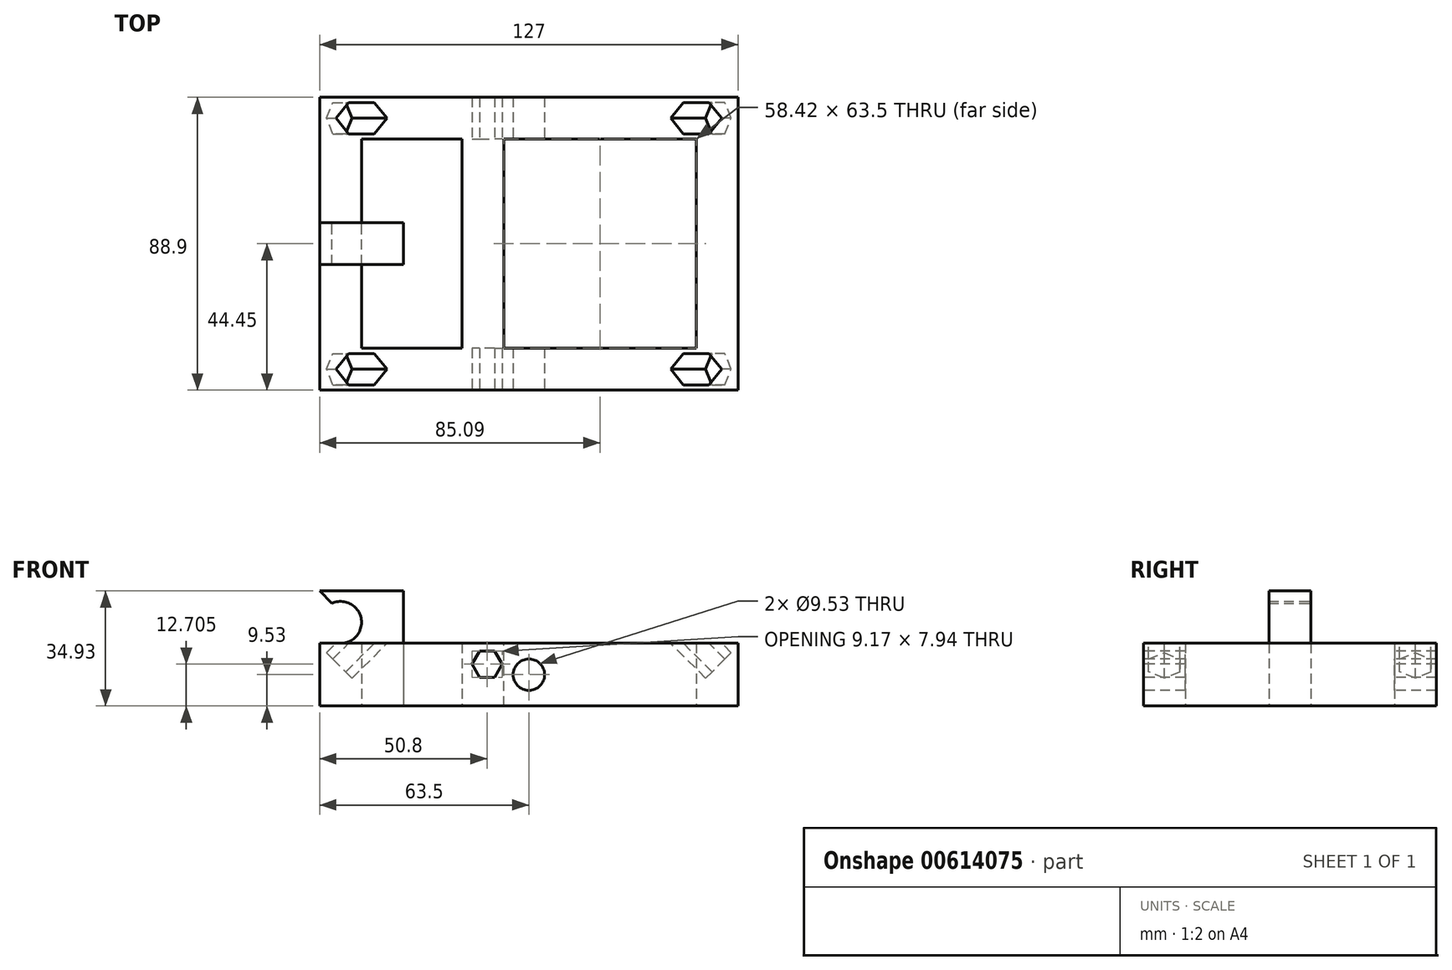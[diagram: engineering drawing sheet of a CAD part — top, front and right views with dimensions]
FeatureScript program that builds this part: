
annotation { "Feature Type Name" : "Feature", "Feature Type Description" : "" }
export const myFeature = defineFeature(function(context is Context, id is Id, definition is map)
    precondition{}
    {
        {
            var Q0;
            Q0=qCreatedBy(makeId("Top.planeOp"),FACE);
            var sketch = newSketch(context, id + "F0", { "sketchPlane" : qUnion([Q0])});
            skLineSegment(sketch, "E0.bottom", {"start": v(63.5, -44.45) * mm, "end": v(-63.5, -44.45) * mm});
            skLineSegment(sketch, "E0.top", {"start": v(63.5, 44.45) * mm, "end": v(-63.5, 44.45) * mm});
            skLineSegment(sketch, "E0.left", {"start": v(63.5, -44.45) * mm, "end": v(63.5, 44.45) * mm});
            skLineSegment(sketch, "E0.right", {"start": v(-63.5, -44.45) * mm, "end": v(-63.5, 44.45) * mm});
            skPoint(sketch, "E0.middle", {"position": v(0, 0) * mm});
            skLineSegment(sketch, "E1.bottom", {"start": v(50.8, -31.75) * mm, "end": v(-50.8, -31.75) * mm});
            skLineSegment(sketch, "E1.top", {"start": v(50.8, 31.75) * mm, "end": v(-50.8, 31.75) * mm});
            skLineSegment(sketch, "E1.left", {"start": v(50.8, -31.75) * mm, "end": v(50.8, 31.75) * mm});
            skLineSegment(sketch, "E1.right", {"start": v(-50.8, -31.75) * mm, "end": v(-50.8, 31.75) * mm});
            skLineSegment(sketch, "E2", {"start": v(0, -62.32) * mm, "end": v(0, 53.23) * mm});
            skPoint(sketch, "E2.endSnap0", {"position": v(0, 44.45) * mm});
            skLineSegment(sketch, "E3.bottom", {"start": v(-50.8, 6.35) * mm, "end": v(-38.1, 6.35) * mm});
            skLineSegment(sketch, "E3.top", {"start": v(-50.8, -6.35) * mm, "end": v(-38.1, -6.35) * mm});
            skLineSegment(sketch, "E3.left", {"start": v(-50.8, 6.35) * mm, "end": v(-50.8, -6.35) * mm});
            skLineSegment(sketch, "E3.right", {"start": v(-38.1, 6.35) * mm, "end": v(-38.1, -6.35) * mm});
            skSolve(sketch);
        }
        {
            var Q0;
            {var subQ4=sQuery(id+"F0.wireOp",EDGE,"E0.right");Q0=makeQuery(id+"F0.imprint","IMPRINT",FACE,{"disambiguationData":[TD([[makeQuery(id+"F0.imprint","IMPRINT",EDGE,{"derivedFrom":subQ4}),-1.0]])]});}
            extrude(context, id + "F1", {"entities" : qUnion([Q0]), "endBound" : BoundingType.SYMMETRIC, "depth" : 19.05 * mm, "offsetDistance" : 25.4 * mm});
        }
        {
            var Q0;
            Q0=qCreatedBy(makeId("Front.planeOp"),FACE);
            var sketch = newSketch(context, id + "F2", { "sketchPlane" : qUnion([Q0])});
            skCircle(sketch, "E4", {"center": v(0, 0) * mm, "radius": 4.76 * mm});
            skCircle(sketch, "E5.cCircle", {"center": v(-12.7, 3.17) * mm, "radius": 3.97 * mm, "construction": true});
            skLineSegment(sketch, "E5.0", {"start": v(-8.12, 3.18) * mm, "end": v(-10.4, -0.8) * mm});
            skLineSegment(sketch, "E5.1", {"start": v(-10.4, -0.8) * mm, "end": v(-15, -0.8) * mm});
            skLineSegment(sketch, "E5.2", {"start": v(-15, -0.8) * mm, "end": v(-17.28, 3.18) * mm});
            skLineSegment(sketch, "E5.3", {"start": v(-17.28, 3.18) * mm, "end": v(-15, 7.14) * mm});
            skLineSegment(sketch, "E5.4", {"start": v(-15, 7.14) * mm, "end": v(-10.4, 7.14) * mm});
            skLineSegment(sketch, "E5.5", {"start": v(-10.4, 7.14) * mm, "end": v(-8.12, 3.18) * mm});
            skPoint(sketch, "E5.0.midPoint", {"position": v(-9.26, 1.2) * mm});
            skSolve(sketch);
        }
        {
            var Q0;
            Q0=makeQuery(id+"F1.opExtrude","CAP_FACE",FACE,{"disambiguationData":[OSD([sQuery(id+"F0.wireOp",EDGE,"E0.bottom"),sQuery(id+"F0.wireOp",EDGE,"E0.top"),sQuery(id+"F0.wireOp",EDGE,"E0.left"),sQuery(id+"F0.wireOp",EDGE,"E0.right"),sQuery(id+"F0.wireOp",EDGE,"E1.bottom"),sQuery(id+"F0.wireOp",EDGE,"E1.top"),sQuery(id+"F0.wireOp",EDGE,"E1.left"),sQuery(id+"F0.wireOp",EDGE,"E1.right")])],"isStart":false});
            var sketch = newSketch(context, id + "F3", { "sketchPlane" : qUnion([Q0])});
            skLineSegment(sketch, "E6", {"start": v(-50.8, -74.19) * mm, "end": v(-50.8, 71.45) * mm, "construction": true});
            skLineSegment(sketch, "E7", {"start": v(50.8, -77.19) * mm, "end": v(50.8, 76.16) * mm, "construction": true});
            skSolve(sketch);
        }
        {
            var Q0;
            Q0=sQuery(id+"F3.wireOp",EDGE,"E6");
            cPlane(context, id + "F4", {"entities" : qUnion([Q0]), "cplaneType" : CPlaneType.LINE_ANGLE, "offset" : 25.4 * mm, "angle" : 315 * degree, "oppositeDirection" : true, "width" : 152.4 * mm, "height" : 152.4 * mm});
        }
        {
            var Q0;
            Q0=qCreatedBy(id+"F4.planeOp",FACE);
            var sketch = newSketch(context, id + "F5", { "sketchPlane" : qUnion([Q0])});
            skCircle(sketch, "E8.cCircle", {"center": v(-38.1, 42.66) * mm, "radius": 4.76 * mm, "construction": true});
            skLineSegment(sketch, "E8.0", {"start": v(-38.1, 37.16) * mm, "end": v(-42.86, 39.9) * mm});
            skLineSegment(sketch, "E8.1", {"start": v(-42.86, 39.9) * mm, "end": v(-42.86, 45.4) * mm});
            skLineSegment(sketch, "E8.2", {"start": v(-42.86, 45.4) * mm, "end": v(-38.1, 48.16) * mm});
            skLineSegment(sketch, "E8.3", {"start": v(-38.1, 48.16) * mm, "end": v(-33.34, 45.4) * mm});
            skLineSegment(sketch, "E8.4", {"start": v(-33.34, 45.4) * mm, "end": v(-33.34, 39.9) * mm});
            skLineSegment(sketch, "E8.5", {"start": v(-33.34, 39.9) * mm, "end": v(-38.1, 37.16) * mm});
            skPoint(sketch, "E8.0.midPoint", {"position": v(-40.48, 38.53) * mm});
            skCircle(sketch, "E9.cCircle", {"center": v(38.1, 42.66) * mm, "radius": 4.76 * mm, "construction": true});
            skLineSegment(sketch, "E9.0", {"start": v(38.1, 37.16) * mm, "end": v(33.34, 39.9) * mm});
            skLineSegment(sketch, "E9.1", {"start": v(33.34, 39.9) * mm, "end": v(33.34, 45.4) * mm});
            skLineSegment(sketch, "E9.2", {"start": v(33.34, 45.4) * mm, "end": v(38.1, 48.16) * mm});
            skLineSegment(sketch, "E9.3", {"start": v(38.1, 48.16) * mm, "end": v(42.86, 45.4) * mm});
            skLineSegment(sketch, "E9.4", {"start": v(42.86, 45.4) * mm, "end": v(42.86, 39.9) * mm});
            skLineSegment(sketch, "E9.5", {"start": v(42.86, 39.9) * mm, "end": v(38.1, 37.16) * mm});
            skPoint(sketch, "E9.0.midPoint", {"position": v(35.72, 38.53) * mm});
            skSolve(sketch);
        }
        {
            var Q0;
            Q0=makeQuery(id+"F5.imprint","IMPRINT",FACE,{"disambiguationData":[TD([[makeQuery(id+"F5.imprint","IMPRINT",EDGE,{"derivedFrom":sQuery(id+"F5.wireOp",EDGE,"E8.0")}),-1.0]])]});
            var Q1;
            Q1=makeQuery(id+"F5.imprint","IMPRINT",FACE,{"disambiguationData":[TD([[makeQuery(id+"F5.imprint","IMPRINT",EDGE,{"derivedFrom":sQuery(id+"F5.wireOp",EDGE,"E9.0")}),-1.0]])]});
            extrude(context, id + "F6", {"entities" : qUnion([Q0, Q1]), "operationType" : NewBodyOperationType.REMOVE, "endBound" : BoundingType.SYMMETRIC, "oppositeDirection" : true, "depth" : 19.05 * mm, "offsetDistance" : 25.4 * mm});
        }
        {
            var Q0;
            Q0=makeQuery(id+"F1.opExtrude","SWEPT_BODY",BODY,{"disambiguationData":[OSD([sQuery(id+"F0.wireOp",EDGE,"E0.bottom"),sQuery(id+"F0.wireOp",EDGE,"E0.top"),sQuery(id+"F0.wireOp",EDGE,"E0.right"),sQuery(id+"F0.wireOp",EDGE,"E1.bottom"),sQuery(id+"F0.wireOp",EDGE,"E1.top"),sQuery(id+"F0.wireOp",EDGE,"E1.right"),sQuery(id+"F0.wireOp",EDGE,"E2")])]});
            var Q1;
            Q1=qCreatedBy(makeId("Right.planeOp"),FACE);
            mirror(context, id + "F7", {"operationType" : NewBodyOperationType.ADD, "entities" : qUnion([Q0]), "mirrorPlane" : qUnion([Q1])});
        }
        {
            var Q0;
            Q0=makeQuery(id+"F2.imprint","IMPRINT",FACE,{"disambiguationData":[TD([[makeQuery(id+"F2.imprint","IMPRINT",EDGE,{"derivedFrom":sQuery(id+"F2.wireOp",EDGE,"E4")}),1.0]])]});
            var Q1;
            Q1=makeQuery(id+"F2.imprint","IMPRINT",FACE,{"disambiguationData":[TD([[makeQuery(id+"F2.imprint","IMPRINT",EDGE,{"derivedFrom":sQuery(id+"F2.wireOp",EDGE,"E5.0")}),-1.0]])]});
            extrude(context, id + "F8", {"entities" : qUnion([Q0, Q1]), "operationType" : NewBodyOperationType.REMOVE, "endBound" : BoundingType.SYMMETRIC, "oppositeDirection" : true, "depth" : 160.02 * mm, "offsetDistance" : 25.4 * mm});
        }
        {
            var Q0;
            {var subQ0=makeQuery(id+"F1.opExtrude","SWEPT_FACE",FACE,{"disambiguationData":[OSD([sQuery(id+"F0.wireOp",EDGE,"E1.top")])]});Q0=makeQuery(id+"F7.boolean.opBoolean","MERGE",FACE,{"derivedFrom":[subQ0,makeQuery(id+"F7.opPattern","COPY",FACE,{"derivedFrom":subQ0,"instanceName":"1"})]});}
            var sketch = newSketch(context, id + "F9", { "sketchPlane" : qUnion([Q0])});
            skLineSegment(sketch, "E10", {"start": v(-20.32, 9.53) * mm, "end": v(-20.32, -9.53) * mm});
            skLineSegment(sketch, "E11", {"start": v(-7.62, -9.53) * mm, "end": v(-7.62, 9.53) * mm});
            skLineSegment(sketch, "E12", {"start": v(-7.62, 9.53) * mm, "end": v(-20.32, 9.53) * mm});
            skLineSegment(sketch, "E13", {"start": v(-20.32, -9.53) * mm, "end": v(-7.62, -9.53) * mm});
            skLineSegment(sketch, "E14", {"start": v(-17.28, 3.18) * mm, "end": v(-15, 7.14) * mm});
            skLineSegment(sketch, "E15", {"start": v(-15, 7.14) * mm, "end": v(-10.4, 7.14) * mm});
            skLineSegment(sketch, "E16", {"start": v(-10.4, 7.14) * mm, "end": v(-8.12, 3.18) * mm});
            skLineSegment(sketch, "E17", {"start": v(-8.12, 3.18) * mm, "end": v(-10.4, -0.8) * mm});
            skLineSegment(sketch, "E18", {"start": v(-10.4, -0.8) * mm, "end": v(-15, -0.8) * mm});
            skLineSegment(sketch, "E19", {"start": v(-15, -0.8) * mm, "end": v(-17.28, 3.18) * mm});
            skSolve(sketch);
        }
        {
            var Q0;
            Q0=makeQuery(id+"F9.imprint","IMPRINT",FACE,{"disambiguationData":[TD([[makeQuery(id+"F9.imprint","IMPRINT",EDGE,{"derivedFrom":sQuery(id+"F9.wireOp",EDGE,"E10")}),1.0]])]});
            var Q1;
            Q1=makeQuery(id+"F9.imprint","IMPRINT",FACE,{"disambiguationData":[TD([[makeQuery(id+"F9.imprint","IMPRINT",EDGE,{"derivedFrom":sQuery(id+"F9.wireOp",EDGE,"E14")}),-1.0]])]});
            extrude(context, id + "F10", {"entities" : qUnion([Q0, Q1]), "operationType" : NewBodyOperationType.ADD, "depth" : 63.5 * mm, "offsetDistance" : 25.4 * mm});
        }
        {
            var Q0;
            Q0=makeQuery(id+"F0.imprint","IMPRINT",FACE,{"disambiguationData":[TD([[makeQuery(id+"F0.imprint","IMPRINT",EDGE,{"derivedFrom":sQuery(id+"F0.wireOp",EDGE,"E3.bottom")}),-1.0]])]});
            extrude(context, id + "F11", {"entities" : qUnion([Q0]), "operationType" : NewBodyOperationType.ADD, "depth" : 25.4 * mm, "offsetDistance" : 25.4 * mm});
        }
        {
            var Q0;
            Q0=makeQuery(id+"F11.opExtrude","SWEPT_FACE",FACE,{"disambiguationData":[OSD([sQuery(id+"F0.wireOp",EDGE,"E3.bottom")])]});
            var sketch = newSketch(context, id + "F12", { "sketchPlane" : qUnion([Q0])});
            skLineSegment(sketch, "E20.bottom", {"start": v(50.8, 9.53) * mm, "end": v(63.5, 9.53) * mm});
            skLineSegment(sketch, "E20.top", {"start": v(50.8, 25.4) * mm, "end": v(63.5, 25.4) * mm});
            skLineSegment(sketch, "E20.left", {"start": v(50.8, 9.53) * mm, "end": v(50.8, 25.4) * mm});
            skLineSegment(sketch, "E20.right", {"start": v(63.5, 9.53) * mm, "end": v(63.5, 25.4) * mm});
            skCircle(sketch, "E21", {"center": v(57.15, 15.88) * mm, "radius": 6.35 * mm});
            skLineSegment(sketch, "E22", {"start": v(63.5, 25.4) * mm, "end": v(59.76, 21.66) * mm});
            skSolve(sketch);
        }
        {
            var Q0;
            {var subQ1=sQuery(id+"F12.wireOp",EDGE,"E20.bottom");var subQ6=sQuery(id+"F12.wireOp",EDGE,"E21");var subQ7=makeQuery(id+"F12.imprint","INTERSECT",VERTEX,{"derivedFrom":[subQ1,subQ6]});Q0=makeQuery(id+"F12.imprint","IMPRINT",FACE,{"disambiguationData":[TD([[makeQuery(id+"F12.imprint","IMPRINT",EDGE,{"disambiguationData":[TD([[subQ7,1.0]])],"derivedFrom":subQ6}),-1.0]])]});}
            var Q1;
            {var subQ0=sQuery(id+"F12.wireOp",EDGE,"E20.top");Q1=makeQuery(id+"F12.imprint","IMPRINT",FACE,{"disambiguationData":[TD([[makeQuery(id+"F12.imprint","IMPRINT",EDGE,{"derivedFrom":subQ0}),-1.0]])]});}
            extrude(context, id + "F13", {"entities" : qUnion([Q0, Q1]), "operationType" : NewBodyOperationType.ADD, "oppositeDirection" : true, "depth" : 12.7 * mm, "offsetDistance" : 25.4 * mm});
        }
        {
            var Q0;
            Q0=makeQuery(id+"F0.imprint","IMPRINT",FACE,{"disambiguationData":[TD([[makeQuery(id+"F0.imprint","IMPRINT",EDGE,{"derivedFrom":sQuery(id+"F0.wireOp",EDGE,"E3.bottom")}),-1.0]])]});
            extrude(context, id + "F14", {"entities" : qUnion([Q0]), "operationType" : NewBodyOperationType.ADD, "oppositeDirection" : true, "depth" : 9.52 * mm, "offsetDistance" : 25.4 * mm});
        }
    });
